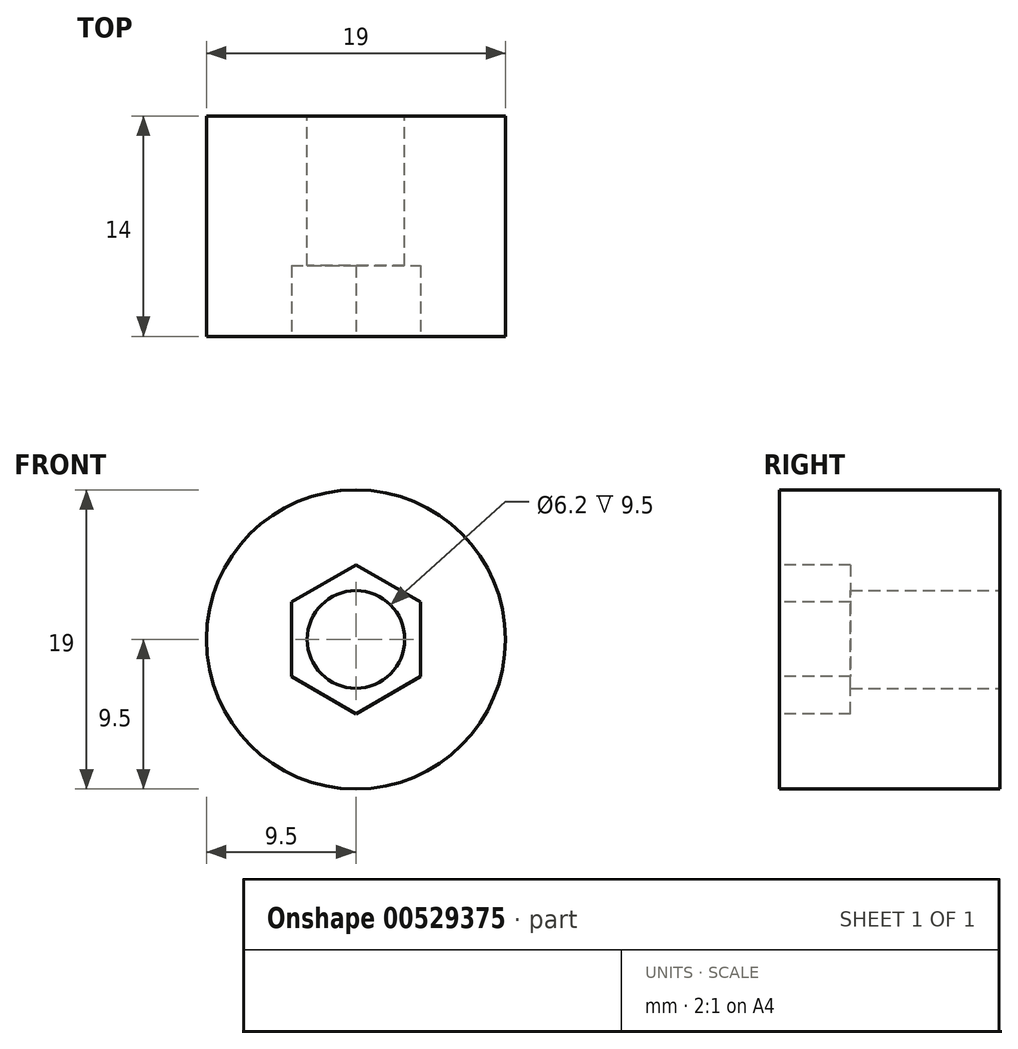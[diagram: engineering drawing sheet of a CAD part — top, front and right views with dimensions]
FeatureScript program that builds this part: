
annotation { "Feature Type Name" : "Feature", "Feature Type Description" : "" }
export const myFeature = defineFeature(function(context is Context, id is Id, definition is map)
    precondition{}
    {
        {
            var Q0;
            Q0=qCreatedBy(makeId("Front.planeOp"),FACE);
            var sketch = newSketch(context, id + "F0", { "sketchPlane" : qUnion([Q0])});
            skCircle(sketch, "E0", {"center": v(0, 0) * mm, "radius": 9.5 * mm});
            skCircle(sketch, "E1", {"center": v(0, 0) * mm, "radius": 3.1 * mm});
            skCircle(sketch, "E2.cCircle", {"center": v(0, 0) * mm, "radius": 4.2 * mm, "construction": true});
            skLineSegment(sketch, "E2.0", {"start": v(4.2, 2.42) * mm, "end": v(4.2, -2.42) * mm});
            skLineSegment(sketch, "E2.1", {"start": v(4.2, -2.42) * mm, "end": v(0, -4.85) * mm});
            skLineSegment(sketch, "E2.2", {"start": v(0, -4.85) * mm, "end": v(-4.2, -2.42) * mm});
            skLineSegment(sketch, "E2.3", {"start": v(-4.2, -2.42) * mm, "end": v(-4.2, 2.42) * mm});
            skLineSegment(sketch, "E2.4", {"start": v(-4.2, 2.42) * mm, "end": v(0, 4.85) * mm});
            skLineSegment(sketch, "E2.5", {"start": v(0, 4.85) * mm, "end": v(4.2, 2.42) * mm});
            skPoint(sketch, "E2.0.midPoint", {"position": v(4.2, 0) * mm});
            skSolve(sketch);
        }
        {
            var Q0;
            Q0=makeQuery(id+"F0.imprint","IMPRINT",FACE,{"disambiguationData":[TD([[makeQuery(id+"F0.imprint","IMPRINT",EDGE,{"derivedFrom":sQuery(id+"F0.wireOp",EDGE,"E0")}),1.0]])]});
            var Q1;
            Q1=makeQuery(id+"F0.imprint","IMPRINT",FACE,{"disambiguationData":[TD([[makeQuery(id+"F0.imprint","IMPRINT",EDGE,{"derivedFrom":sQuery(id+"F0.wireOp",EDGE,"E1")}),-1.0]])]});
            extrude(context, id + "F1", {"entities" : qUnion([Q0, Q1]), "depth" : 14 * mm, "offsetDistance" : 25 * mm});
        }
        {
            var Q0;
            Q0=makeQuery(id+"F1.opExtrude","CAP_FACE",FACE,{"disambiguationData":[OSD([sQuery(id+"F0.wireOp",EDGE,"E0"),sQuery(id+"F0.wireOp",EDGE,"E1")])],"isStart":false});
            var sketch = newSketch(context, id + "F2", { "sketchPlane" : qUnion([Q0])});
            skLineSegment(sketch, "E3", {"start": v(0, 0) * mm, "end": v(4.1, 0) * mm});
            skCircle(sketch, "E4.cCircle", {"center": v(0, 0) * mm, "radius": 4.1 * mm, "construction": true});
            skLineSegment(sketch, "E4.0", {"start": v(4.1, 2.37) * mm, "end": v(4.1, -2.37) * mm});
            skLineSegment(sketch, "E4.1", {"start": v(4.1, -2.37) * mm, "end": v(0, -4.73) * mm});
            skLineSegment(sketch, "E4.2", {"start": v(0, -4.73) * mm, "end": v(-4.1, -2.37) * mm});
            skLineSegment(sketch, "E4.3", {"start": v(-4.1, -2.37) * mm, "end": v(-4.1, 2.37) * mm});
            skLineSegment(sketch, "E4.4", {"start": v(-4.1, 2.37) * mm, "end": v(0, 4.73) * mm});
            skLineSegment(sketch, "E4.5", {"start": v(0, 4.73) * mm, "end": v(4.1, 2.37) * mm});
            skPoint(sketch, "E4.0.midPoint", {"position": v(4.1, 0) * mm});
            skSolve(sketch);
        }
        {
            var Q0;
            {var subQ0=sQuery(id+"F2.wireOp",EDGE,"E4.1");Q0=makeQuery(id+"F2.imprint","IMPRINT",FACE,{"disambiguationData":[TD([[makeQuery(id+"F2.imprint","IMPRINT",EDGE,{"derivedFrom":subQ0}),-1.0]])]});}
            extrude(context, id + "F3", {"entities" : qUnion([Q0]), "operationType" : NewBodyOperationType.REMOVE, "oppositeDirection" : true, "depth" : 4.5 * mm, "offsetDistance" : 25 * mm});
        }
    });
